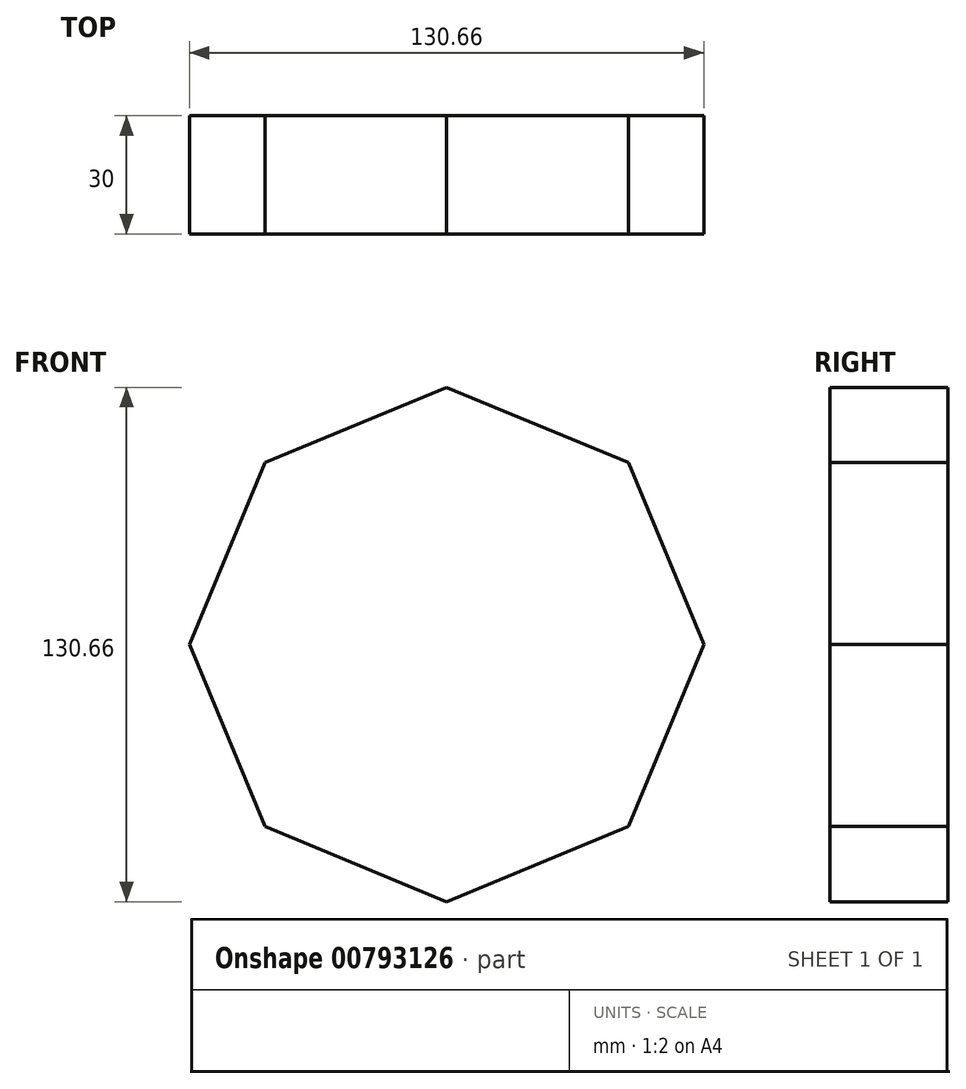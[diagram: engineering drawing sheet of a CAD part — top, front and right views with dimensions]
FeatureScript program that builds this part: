
annotation { "Feature Type Name" : "Feature", "Feature Type Description" : "" }
export const myFeature = defineFeature(function(context is Context, id is Id, definition is map)
    precondition{}
    {
        {
            var Q0;
            Q0=qCreatedBy(makeId("Front.planeOp"),FACE);
            var sketch = newSketch(context, id + "F0", { "sketchPlane" : qUnion([Q0])});
            skCircle(sketch, "E0.cCircle", {"center": v(0, 0) * mm, "radius": 65.33 * mm, "construction": true});
            skLineSegment(sketch, "E0.0", {"start": v(0, 65.33) * mm, "end": v(46.2, 46.2) * mm});
            skLineSegment(sketch, "E0.1", {"start": v(46.2, 46.2) * mm, "end": v(65.33, 0) * mm});
            skLineSegment(sketch, "E0.2", {"start": v(65.33, 0) * mm, "end": v(46.2, -46.2) * mm});
            skLineSegment(sketch, "E0.3", {"start": v(46.2, -46.2) * mm, "end": v(0, -65.33) * mm});
            skLineSegment(sketch, "E0.4", {"start": v(0, -65.33) * mm, "end": v(-46.2, -46.2) * mm});
            skLineSegment(sketch, "E0.5", {"start": v(-46.2, -46.2) * mm, "end": v(-65.33, 0) * mm});
            skLineSegment(sketch, "E0.6", {"start": v(-65.33, 0) * mm, "end": v(-46.2, 46.2) * mm});
            skLineSegment(sketch, "E0.7", {"start": v(-46.2, 46.2) * mm, "end": v(0, 65.33) * mm});
            skSolve(sketch);
        }
        {
            var Q0;
            Q0=makeQuery(id+"F0.imprint","IMPRINT",FACE,{"disambiguationData":[TD([[makeQuery(id+"F0.imprint","IMPRINT",EDGE,{"derivedFrom":sQuery(id+"F0.wireOp",EDGE,"E0.0")}),-1.0]])]});
            extrude(context, id + "F1", {"entities" : qUnion([Q0]), "depth" : 30 * mm, "offsetDistance" : 25 * mm});
        }
    });
